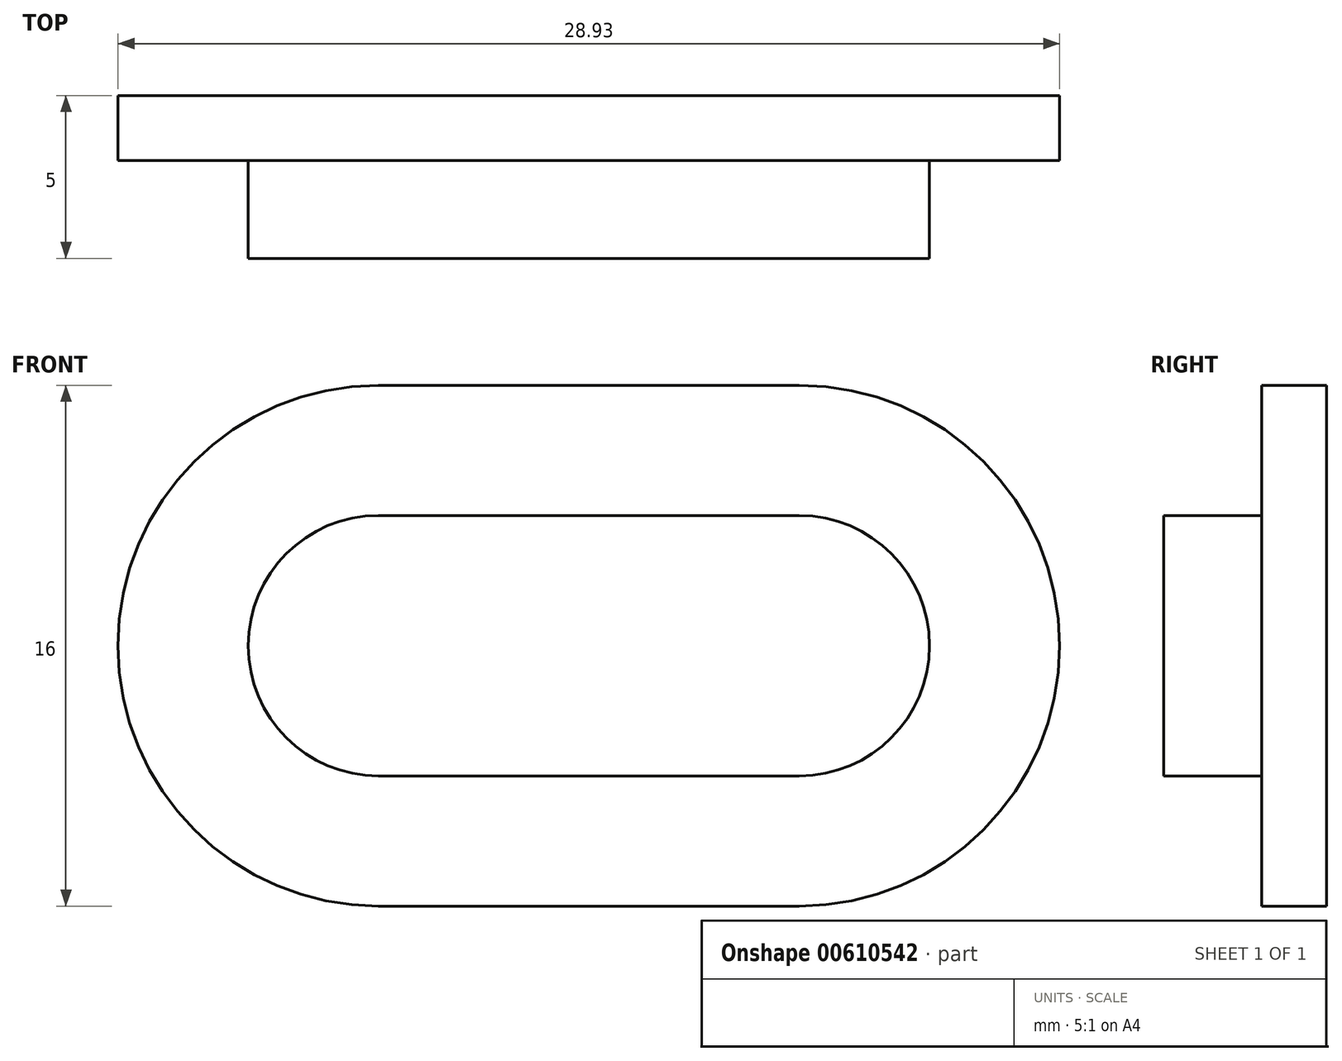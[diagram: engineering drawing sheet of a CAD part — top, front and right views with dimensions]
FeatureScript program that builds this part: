
annotation { "Feature Type Name" : "Feature", "Feature Type Description" : "" }
export const myFeature = defineFeature(function(context is Context, id is Id, definition is map)
    precondition{}
    {
        {
            var Q0;
            Q0=qCreatedBy(makeId("Front.planeOp"),FACE);
            var sketch = newSketch(context, id + "F0", { "sketchPlane" : qUnion([Q0])});
            skLineSegment(sketch, "E0.bottom", {"start": v(6.5, -8) * mm, "end": v(-6.43, -8) * mm});
            skLineSegment(sketch, "E0.top", {"start": v(6.5, 8) * mm, "end": v(-6.43, 8) * mm});
            skPoint(sketch, "E0.middle", {"position": v(0, 0) * mm});
            skArc(sketch, "E1", {"start": v(6.5, -8) * mm, "mid": v(14.5, 0) * mm, "end": v(6.5, 8) * mm});
            skArc(sketch, "E2", {"start": v(-6.43, 8) * mm, "mid": v(-14.43, 0) * mm, "end": v(-6.43, -8) * mm});
            skPoint(sketch, "E3.orphan", {"position": v(14.5, 8) * mm});
            skPoint(sketch, "E4.orphan", {"position": v(14.5, -8) * mm});
            skPoint(sketch, "E0.right.start.orphan", {"position": v(-14.5, -8) * mm});
            skPoint(sketch, "E5.orphan", {"position": v(-14.5, 8) * mm});
            skLineSegment(sketch, "E6.0", {"start": v(6.5, 4) * mm, "end": v(-6.43, 4) * mm});
            skArc(sketch, "E6.1", {"start": v(6.5, -4) * mm, "mid": v(10.5, 0) * mm, "end": v(6.5, 4) * mm});
            skLineSegment(sketch, "E6.2", {"start": v(6.5, -4) * mm, "end": v(-6.43, -4) * mm});
            skArc(sketch, "E6.3", {"start": v(-6.43, 4) * mm, "mid": v(-10.43, 0) * mm, "end": v(-6.43, -4) * mm});
            skSolve(sketch);
        }
        {
            var Q0;
            Q0=makeQuery(id+"F0.imprint","IMPRINT",FACE,{"disambiguationData":[TD([[makeQuery(id+"F0.imprint","IMPRINT",EDGE,{"derivedFrom":sQuery(id+"F0.wireOp",EDGE,"E6.0")}),1.0]])]});
            var Q1;
            Q1=makeQuery(id+"F0.imprint","IMPRINT",FACE,{"disambiguationData":[TD([[makeQuery(id+"F0.imprint","IMPRINT",EDGE,{"derivedFrom":sQuery(id+"F0.wireOp",EDGE,"E0.bottom")}),-1.0]])]});
            extrude(context, id + "F1", {"entities" : qUnion([Q0, Q1]), "depth" : 2 * mm, "offsetDistance" : 25 * mm});
        }
        {
            var Q0;
            Q0=makeQuery(id+"F0.imprint","IMPRINT",FACE,{"disambiguationData":[TD([[makeQuery(id+"F0.imprint","IMPRINT",EDGE,{"derivedFrom":sQuery(id+"F0.wireOp",EDGE,"E6.0")}),1.0]])]});
            extrude(context, id + "F2", {"entities" : qUnion([Q0]), "operationType" : NewBodyOperationType.ADD, "depth" : 5 * mm, "offsetDistance" : 25 * mm});
        }
    });
